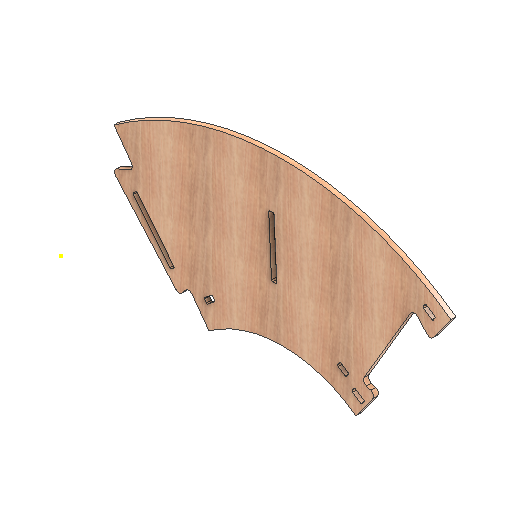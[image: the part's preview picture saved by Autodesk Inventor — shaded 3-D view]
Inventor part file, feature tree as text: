
AUTODESK INVENTOR PART (.ipt)
format: ipt  version: 2021 (Build 250183000, 183)  size: 313,344 bytes
history: native  units: mm
features: other x2, extrude x2, sketch x1, hole x1
ambient origin geometry x8: Origin, YZ Plane, XZ Plane, XY Plane, X Axis, Y Axis, Z Axis, Center Point
bodies: Body1 (feature_tree)
feature tree (6):
  sketch  "Sketch1"  dims[d100=18.0mm d101=0.0mm d102=10.0mm d103=0.0mm]
  other  "CONTOURS"
  hole  "HOLES"  [1 undecoded]
  other  "LETTERS"
  extrude  "Extrusion2"  [1 undecoded]
  extrude  "Extrusion3"  [1 undecoded]
note: 3 required parameter values undecoded (feature->parameter linkage not recoverable at this tier; creation-order binding heuristic only, values carry confidence <= 0.55)
